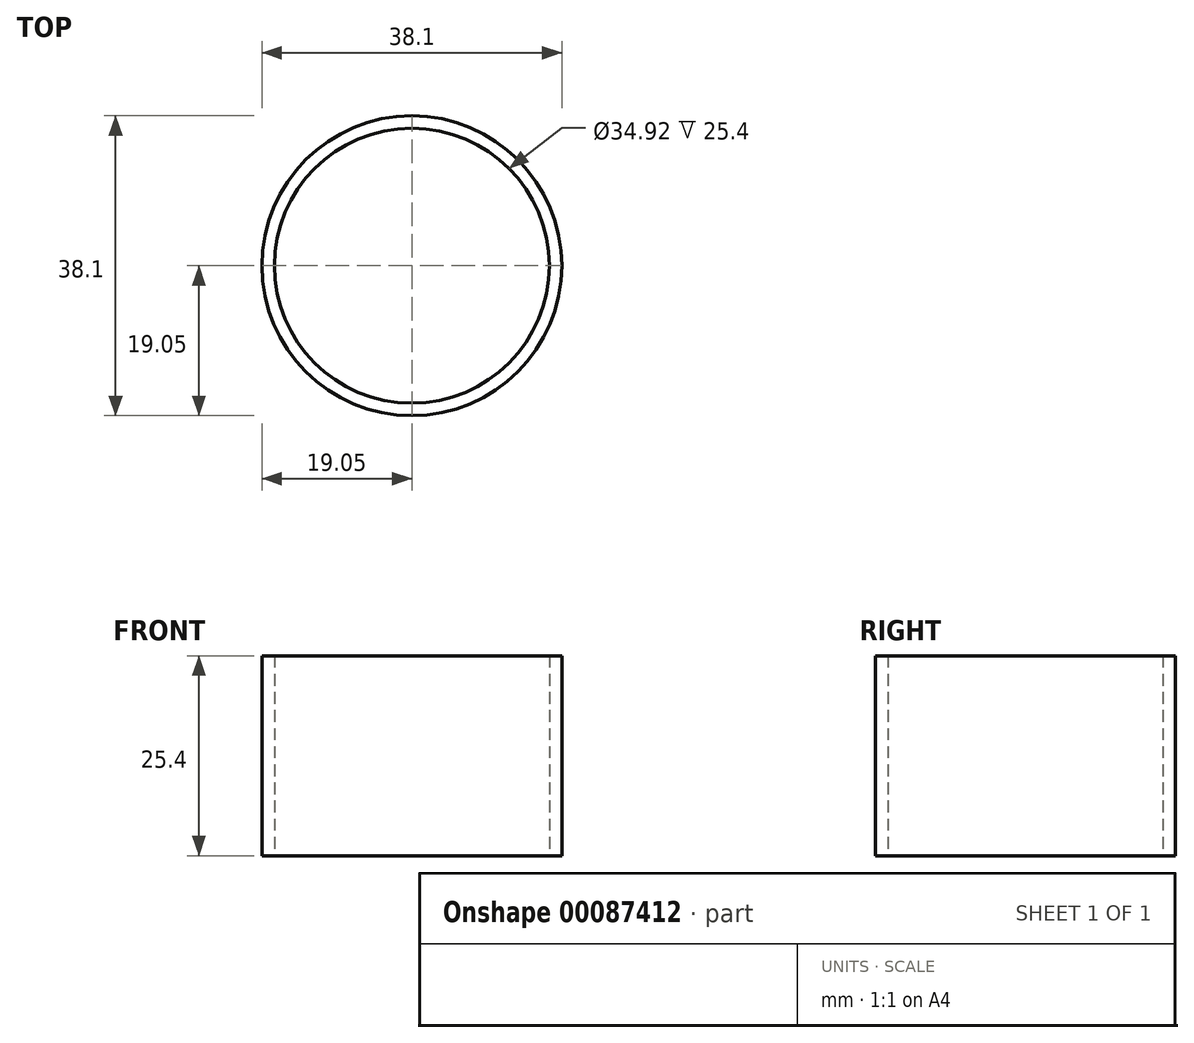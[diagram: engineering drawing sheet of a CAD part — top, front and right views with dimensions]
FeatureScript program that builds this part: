
annotation { "Feature Type Name" : "Feature", "Feature Type Description" : "" }
export const myFeature = defineFeature(function(context is Context, id is Id, definition is map)
    precondition{}
    {
        {
            var Q0;
            Q0=qCreatedBy(makeId("Top.planeOp"),FACE);
            var sketch = newSketch(context, id + "F0", { "sketchPlane" : qUnion([Q0])});
            skCircle(sketch, "E0", {"center": v(0, 0) * mm, "radius": 19.05 * mm});
            skCircle(sketch, "E1.0", {"center": v(0, 0) * mm, "radius": 17.46 * mm});
            skSolve(sketch);
        }
        {
            var Q0;
            Q0 = qSketchRegion(id + "F0", true);
            extrude(context, id + "F1", {"entities" : qUnion([Q0]), "depth" : 25.4 * mm});
        }
    });
